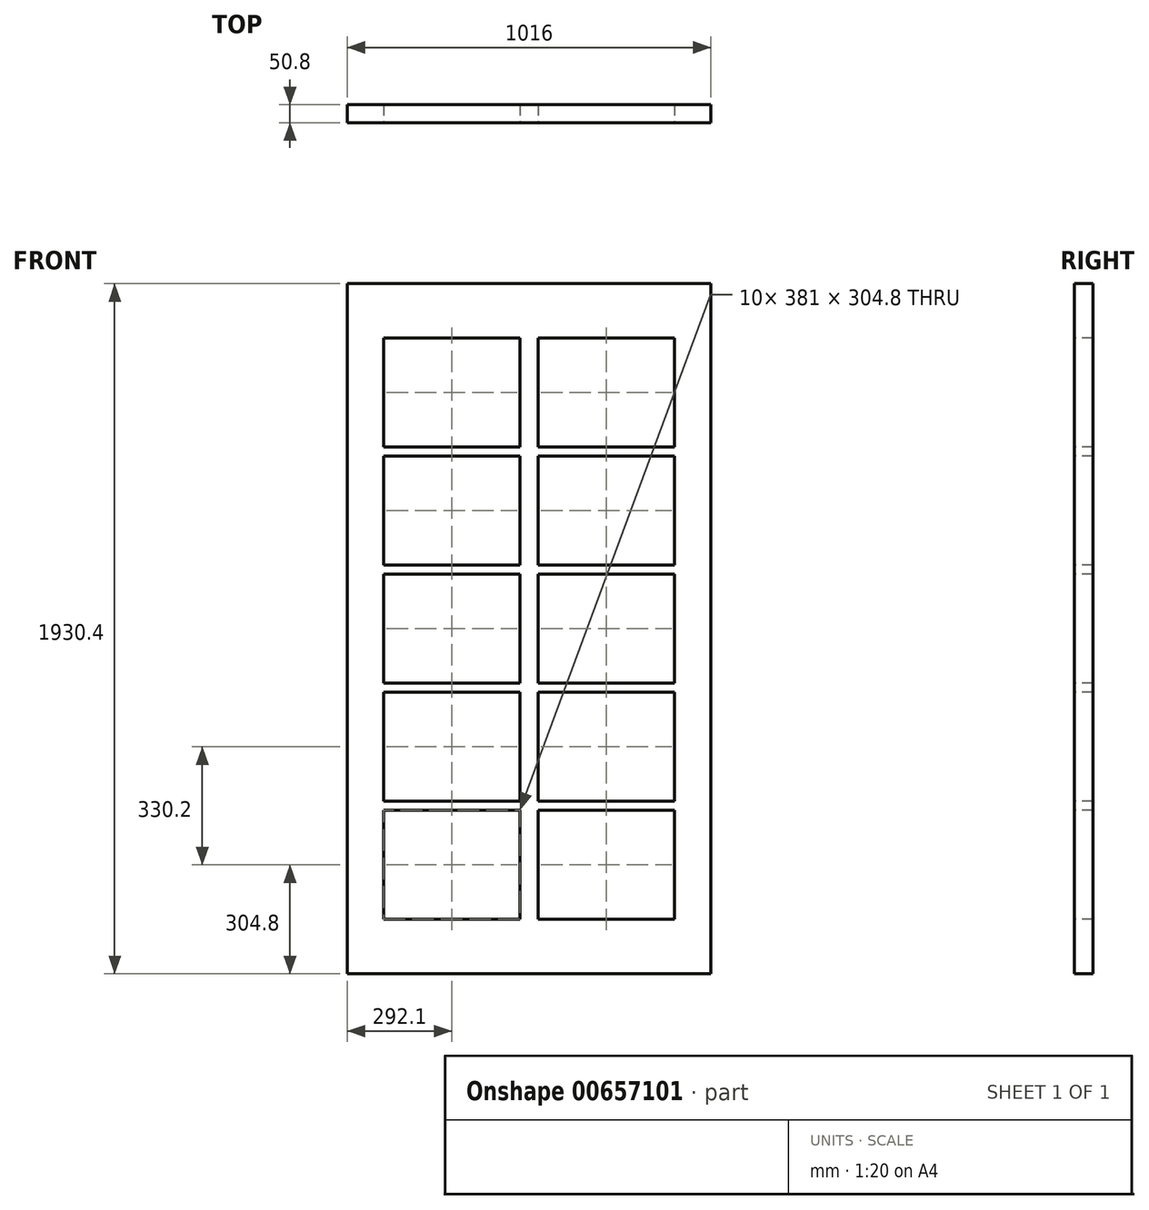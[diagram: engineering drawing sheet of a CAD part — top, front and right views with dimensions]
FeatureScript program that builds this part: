
annotation { "Feature Type Name" : "Feature", "Feature Type Description" : "" }
export const myFeature = defineFeature(function(context is Context, id is Id, definition is map)
    precondition{}
    {
        {
            var Q0;
            Q0=qCreatedBy(makeId("Front.planeOp"),FACE);
            var sketch = newSketch(context, id + "F0", { "sketchPlane" : qUnion([Q0])});
            skLineSegment(sketch, "E0.bottom", {"start": v(-508, 965.2) * mm, "end": v(508, 965.2) * mm});
            skLineSegment(sketch, "E0.top", {"start": v(-508, -965.2) * mm, "end": v(508, -965.2) * mm});
            skLineSegment(sketch, "E0.left", {"start": v(-508, 965.2) * mm, "end": v(-508, -965.2) * mm});
            skLineSegment(sketch, "E0.right", {"start": v(508, 965.2) * mm, "end": v(508, -965.2) * mm});
            skSolve(sketch);
        }
        {
            var Q0;
            Q0=qSketchRegion(id+"F0",true);
            extrude(context, id + "F1", {"entities" : qUnion([Q0]), "depth" : 50.8 * mm, "offsetDistance" : 25.4 * mm});
        }
        {
            var Q0;
            Q0=makeQuery(id+"F1.opExtrude","CAP_FACE",FACE,{"disambiguationData":[OSD([sQuery(id+"F0.wireOp",EDGE,"E0.bottom"),sQuery(id+"F0.wireOp",EDGE,"E0.top"),sQuery(id+"F0.wireOp",EDGE,"E0.left"),sQuery(id+"F0.wireOp",EDGE,"E0.right")])],"isStart":false});
            var sketch = newSketch(context, id + "F2", { "sketchPlane" : qUnion([Q0])});
            skLineSegment(sketch, "E1.bottom", {"start": v(-406.4, 812.8) * mm, "end": v(-25.4, 812.8) * mm});
            skLineSegment(sketch, "E1.top", {"start": v(-406.4, 508) * mm, "end": v(-25.4, 508) * mm});
            skLineSegment(sketch, "E1.left", {"start": v(-406.4, 812.8) * mm, "end": v(-406.4, 508) * mm});
            skLineSegment(sketch, "E1.right", {"start": v(-25.4, 812.8) * mm, "end": v(-25.4, 508) * mm});
            skLineSegment(sketch, "E2.bottom", {"start": v(-406.4, 482.6) * mm, "end": v(-25.4, 482.6) * mm});
            skLineSegment(sketch, "E2.top", {"start": v(-406.4, 177.8) * mm, "end": v(-25.4, 177.8) * mm});
            skLineSegment(sketch, "E2.left", {"start": v(-406.4, 482.6) * mm, "end": v(-406.4, 177.8) * mm});
            skLineSegment(sketch, "E2.right", {"start": v(-25.4, 482.6) * mm, "end": v(-25.4, 177.8) * mm});
            skLineSegment(sketch, "E3.bottom", {"start": v(-406.4, 152.4) * mm, "end": v(-25.4, 152.4) * mm});
            skLineSegment(sketch, "E3.top", {"start": v(-406.4, -152.4) * mm, "end": v(-25.4, -152.4) * mm});
            skLineSegment(sketch, "E3.left", {"start": v(-406.4, 152.4) * mm, "end": v(-406.4, -152.4) * mm});
            skLineSegment(sketch, "E3.right", {"start": v(-25.4, 152.4) * mm, "end": v(-25.4, -152.4) * mm});
            skLineSegment(sketch, "E4.bottom", {"start": v(-406.4, -177.8) * mm, "end": v(-25.4, -177.8) * mm});
            skLineSegment(sketch, "E4.top", {"start": v(-406.4, -482.6) * mm, "end": v(-25.4, -482.6) * mm});
            skLineSegment(sketch, "E4.left", {"start": v(-406.4, -177.8) * mm, "end": v(-406.4, -482.6) * mm});
            skLineSegment(sketch, "E4.right", {"start": v(-25.4, -177.8) * mm, "end": v(-25.4, -482.6) * mm});
            skLineSegment(sketch, "E5.bottom", {"start": v(-406.4, -508) * mm, "end": v(-25.4, -508) * mm});
            skLineSegment(sketch, "E5.top", {"start": v(-406.4, -812.8) * mm, "end": v(-25.4, -812.8) * mm});
            skLineSegment(sketch, "E5.left", {"start": v(-406.4, -508) * mm, "end": v(-406.4, -812.8) * mm});
            skLineSegment(sketch, "E5.right", {"start": v(-25.4, -508) * mm, "end": v(-25.4, -812.8) * mm});
            skLineSegment(sketch, "E6", {"start": v(-406.4, 508) * mm, "end": v(-508, 508) * mm, "construction": true});
            skLineSegment(sketch, "E7", {"start": v(-406.4, 177.8) * mm, "end": v(-508, 177.8) * mm, "construction": true});
            skLineSegment(sketch, "E8", {"start": v(-406.4, -152.4) * mm, "end": v(-508, -152.4) * mm, "construction": true});
            skLineSegment(sketch, "E9", {"start": v(-406.4, -482.6) * mm, "end": v(-508, -482.6) * mm, "construction": true});
            skLineSegment(sketch, "E10", {"start": v(-406.4, -812.8) * mm, "end": v(-508, -812.8) * mm, "construction": true});
            skLineSegment(sketch, "E11", {"start": v(0, 965.2) * mm, "end": v(0, -965.2) * mm, "construction": true});
            skLineSegment(sketch, "E12.MirrorCS", {"start": v(406.4, 482.6) * mm, "end": v(406.4, 177.8) * mm});
            skLineSegment(sketch, "E13.MirrorCS", {"start": v(406.4, 177.8) * mm, "end": v(25.4, 177.8) * mm});
            skLineSegment(sketch, "E14.MirrorCS", {"start": v(406.4, 482.6) * mm, "end": v(25.4, 482.6) * mm});
            skLineSegment(sketch, "E15.MirrorCS", {"start": v(25.4, 482.6) * mm, "end": v(25.4, 177.8) * mm});
            skLineSegment(sketch, "E16.MirrorCS", {"start": v(25.4, 812.8) * mm, "end": v(25.4, 508) * mm});
            skLineSegment(sketch, "E17.MirrorCS", {"start": v(406.4, 812.8) * mm, "end": v(406.4, 508) * mm});
            skLineSegment(sketch, "E18.MirrorCS", {"start": v(406.4, 508) * mm, "end": v(25.4, 508) * mm});
            skLineSegment(sketch, "E19.MirrorCS", {"start": v(406.4, -152.4) * mm, "end": v(25.4, -152.4) * mm});
            skLineSegment(sketch, "E20.MirrorCS", {"start": v(406.4, 812.8) * mm, "end": v(25.4, 812.8) * mm});
            skLineSegment(sketch, "E21.MirrorCS", {"start": v(25.4, -177.8) * mm, "end": v(25.4, -482.6) * mm});
            skLineSegment(sketch, "E22.MirrorCS", {"start": v(406.4, -177.8) * mm, "end": v(406.4, -482.6) * mm});
            skLineSegment(sketch, "E23.MirrorCS", {"start": v(406.4, 152.4) * mm, "end": v(406.4, -152.4) * mm});
            skLineSegment(sketch, "E24.MirrorCS", {"start": v(25.4, 152.4) * mm, "end": v(25.4, -152.4) * mm});
            skLineSegment(sketch, "E25.MirrorCS", {"start": v(406.4, -177.8) * mm, "end": v(25.4, -177.8) * mm});
            skLineSegment(sketch, "E26.MirrorCS", {"start": v(406.4, -482.6) * mm, "end": v(25.4, -482.6) * mm});
            skLineSegment(sketch, "E27.MirrorCS", {"start": v(406.4, -508) * mm, "end": v(406.4, -812.8) * mm});
            skLineSegment(sketch, "E28.MirrorCS", {"start": v(406.4, -508) * mm, "end": v(25.4, -508) * mm});
            skLineSegment(sketch, "E29.MirrorCS", {"start": v(406.4, -812.8) * mm, "end": v(25.4, -812.8) * mm});
            skLineSegment(sketch, "E30.MirrorCS", {"start": v(25.4, -508) * mm, "end": v(25.4, -812.8) * mm});
            skLineSegment(sketch, "E31.MirrorCS", {"start": v(406.4, 152.4) * mm, "end": v(25.4, 152.4) * mm});
            skSolve(sketch);
        }
        {
            var Q0;
            Q0=qSketchRegion(id+"F2",true);
            extrude(context, id + "F3", {"entities" : qUnion([Q0]), "operationType" : NewBodyOperationType.REMOVE, "endBound" : BoundingType.THROUGH_ALL, "oppositeDirection" : true, "depth" : 25.4 * mm, "offsetDistance" : 25.4 * mm});
        }
    });
